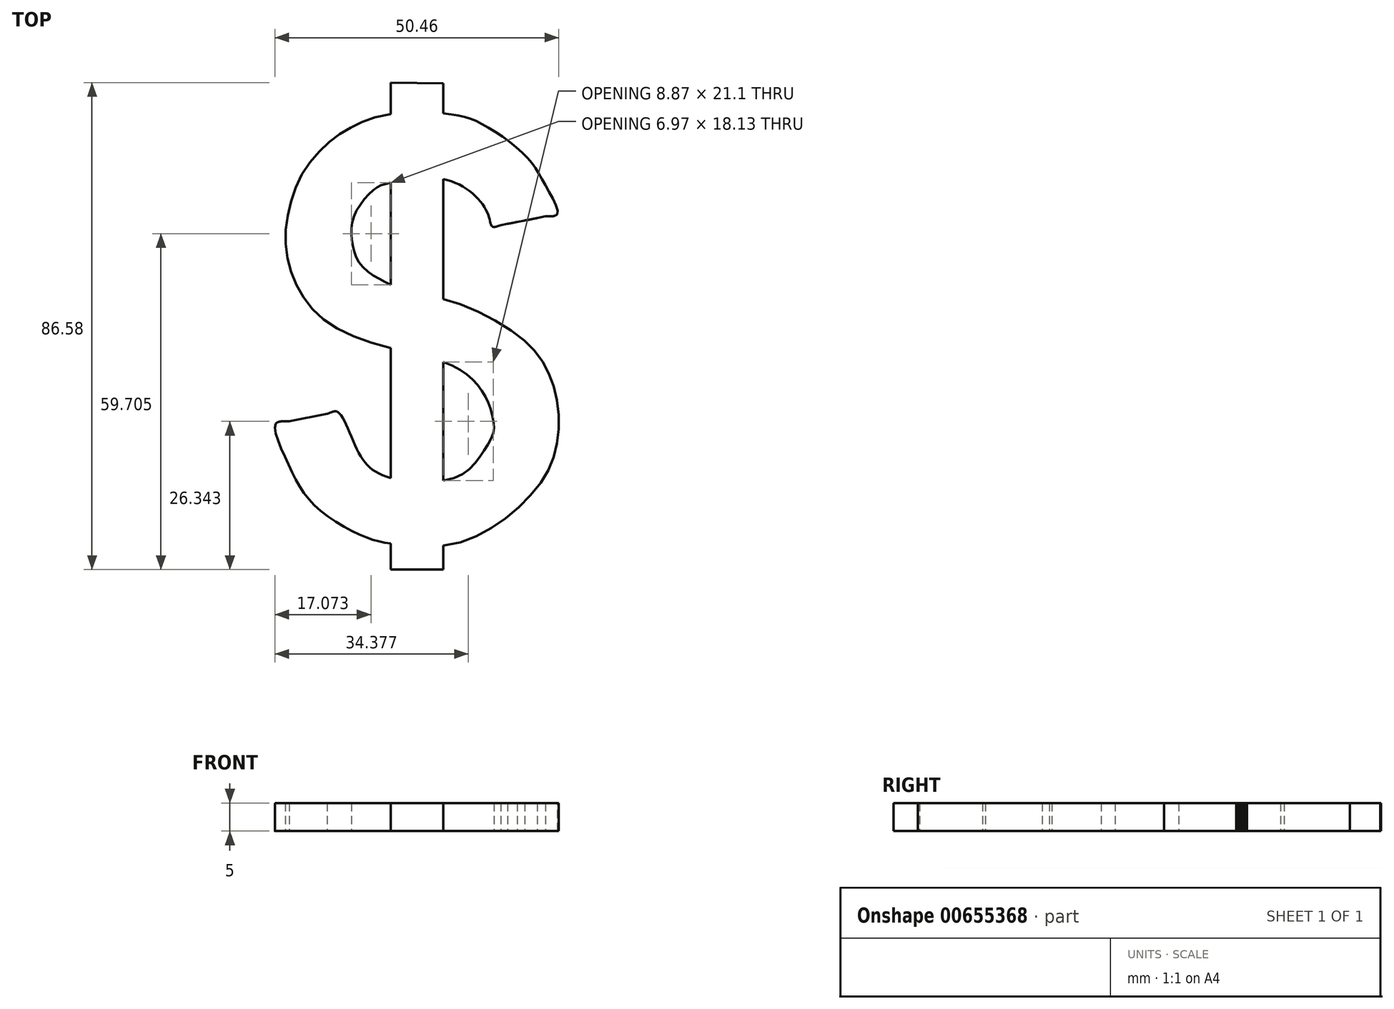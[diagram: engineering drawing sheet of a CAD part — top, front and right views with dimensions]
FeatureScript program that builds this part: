
annotation { "Feature Type Name" : "Feature", "Feature Type Description" : "" }
export const myFeature = defineFeature(function(context is Context, id is Id, definition is map)
    precondition{}
    {
        {
            var Q0;
            Q0=qCreatedBy(makeId("Top.planeOp"),FACE);
            var sketch = newSketch(context, id + "F0", { "sketchPlane" : qUnion([Q0])});
            skLineSegment(sketch, "E0", {"start": v(37.5, 26.82) * mm, "end": v(26.02, 24.57) * mm});
            skLineSegment(sketch, "E1", {"start": v(-1.48, -8.34) * mm, "end": v(-12.5, -10.46) * mm});
            skFitSpline(sketch, "E2", {"points": [v(37.5, 26.82) * mm, v(35.4, 31.97) * mm, v(32.1, 37) * mm, v(24.43, 42.68) * mm, v(18.88, 44.53) * mm, v(7.64, 44.53) * mm, v(1.17, 42.42) * mm, v(-3.6, 39.11) * mm, v(-7.95, 33.7) * mm, v(-10.33, 26.82) * mm, v(-10.6, 19.94) * mm, v(-8.35, 13.33) * mm, v(-3.46, 7.65) * mm, v(7.25, 3.16) * mm, v(18.62, 0) * mm, v(23.37, -3.59) * mm, v(25.49, -7.29) * mm, v(26.15, -9.93) * mm, v(26.15, -12.05) * mm, v(24.17, -15.75) * mm, v(19.54, -19.98) * mm, v(7.12, -19.84) * mm, v(1.96, -15.09) * mm, v(-1.48, -8.34) * mm, v(-3.35, -8.7) * mm, v(-6.99, -9.4) * mm, v(-10.08, -10) * mm, v(-12.5, -10.46) * mm, v(-10.46, -17.2) * mm, v(-5.57, -25) * mm, v(3.68, -30.68) * mm, v(9.1, -31.87) * mm, v(18.75, -31.87) * mm, v(28, -27.51) * mm, v(34.87, -20.5) * mm, v(37.5, -13.9) * mm, v(37.5, -6.5) * mm, v(35.27, 0) * mm, v(30.51, 5.27) * mm, v(19.4, 11.09) * mm, v(11.61, 12.94) * mm, v(7.38, 14.52) * mm, v(2.62, 17.83) * mm, v(1.04, 22.2) * mm, v(1.56, 26.82) * mm, v(5.13, 31.31) * mm, v(7.78, 32.37) * mm, v(18.35, 32.77) * mm, v(25.23, 26.82) * mm, v(26.02, 24.57) * mm, v(27.5, 24.86) * mm, v(28.69, 25.1) * mm, v(30.4, 25.43) * mm, v(31.76, 25.7) * mm, v(33.98, 26.13) * mm, v(35.4, 26.4) * mm, v(37.5, 26.82) * mm]});
            skSolve(sketch);
        }
        {
            var Q0;
            Q0 = qSketchRegion(id + "F0", true);
            extrude(context, id + "F1", {"entities" : qUnion([Q0]), "depth" : 5 * mm, "offsetDistance" : 25 * mm});
        }
        {
            var Q0;
            Q0=qCreatedBy(makeId("Top.planeOp"),FACE);
            var sketch = newSketch(context, id + "F2", { "sketchPlane" : qUnion([Q0])});
            skLineSegment(sketch, "E3", {"start": v(7.9, 50.21) * mm, "end": v(7.9, -36.37) * mm});
            skLineSegment(sketch, "E4", {"start": v(7.9, -36.37) * mm, "end": v(17.3, -36.37) * mm});
            skLineSegment(sketch, "E5", {"start": v(17.3, -36.37) * mm, "end": v(17.3, 50.08) * mm});
            skLineSegment(sketch, "E6", {"start": v(17.3, 50.08) * mm, "end": v(7.9, 50.21) * mm});
            skSolve(sketch);
        }
        {
            var Q0;
            Q0 = qSketchRegion(id + "F2", true);
            extrude(context, id + "F3", {"entities" : qUnion([Q0]), "operationType" : NewBodyOperationType.ADD, "depth" : 5 * mm, "offsetDistance" : 25 * mm});
        }
    });
